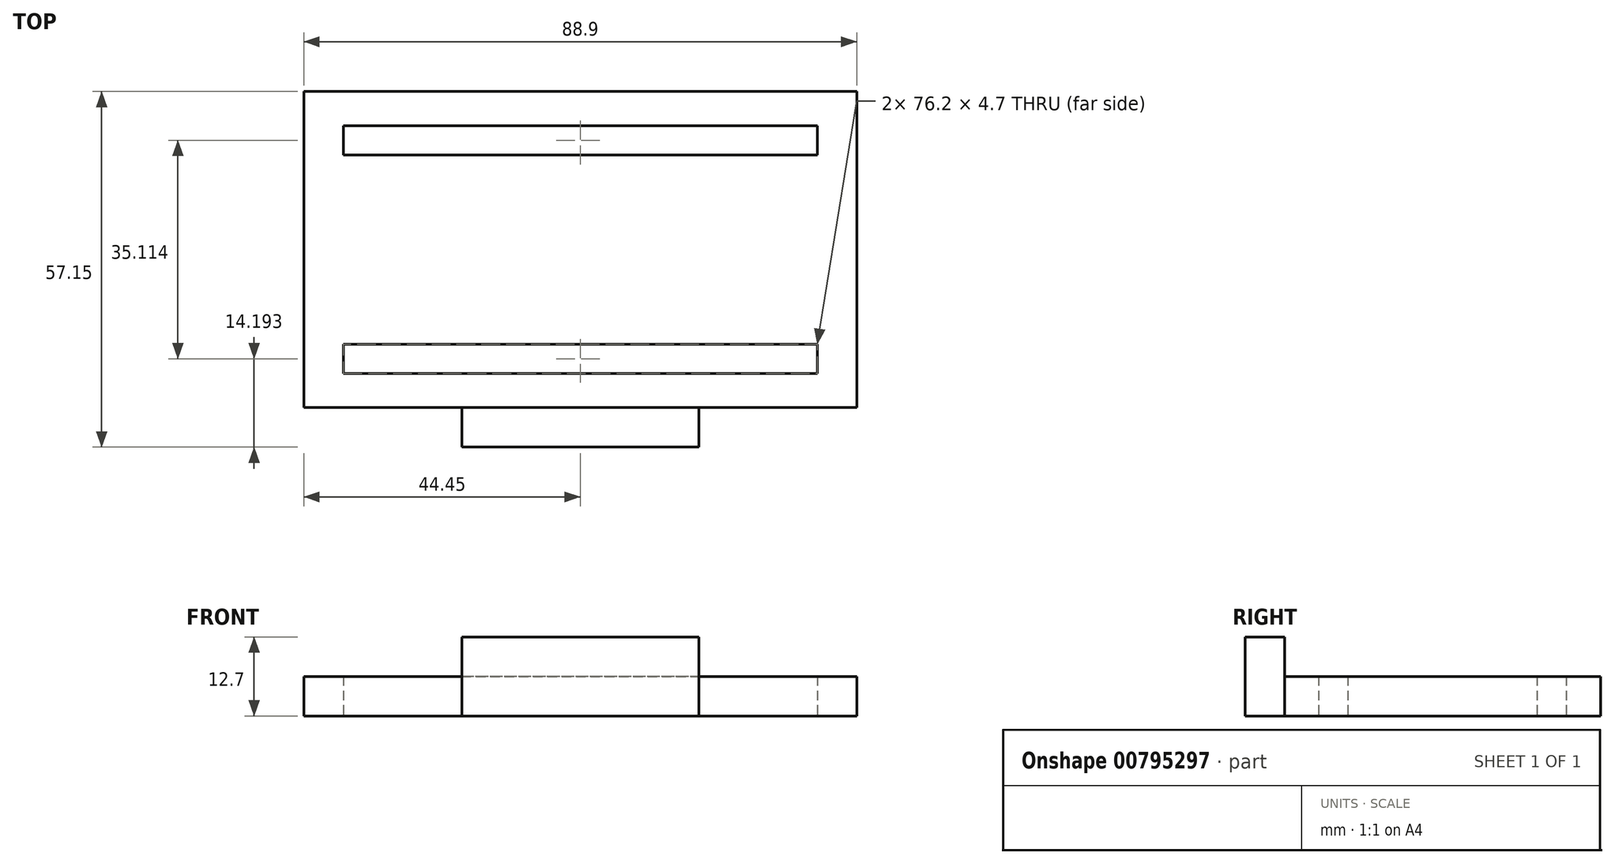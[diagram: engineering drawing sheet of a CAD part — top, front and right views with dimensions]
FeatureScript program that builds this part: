
annotation { "Feature Type Name" : "Feature", "Feature Type Description" : "" }
export const myFeature = defineFeature(function(context is Context, id is Id, definition is map)
    precondition{}
    {
        {
            var Q0;
            Q0=qCreatedBy(makeId("Top.planeOp"),FACE);
            var sketch = newSketch(context, id + "F0", { "sketchPlane" : qUnion([Q0])});
            skLineSegment(sketch, "E0.bottom", {"start": v(44.45, -25.4) * mm, "end": v(-44.45, -25.4) * mm});
            skLineSegment(sketch, "E0.top", {"start": v(44.45, 25.4) * mm, "end": v(-44.45, 25.4) * mm});
            skLineSegment(sketch, "E0.left", {"start": v(44.45, -25.4) * mm, "end": v(44.45, 25.4) * mm});
            skLineSegment(sketch, "E0.right", {"start": v(-44.45, -25.4) * mm, "end": v(-44.45, 25.4) * mm});
            skPoint(sketch, "E0.middle", {"position": v(0, 0) * mm});
            skLineSegment(sketch, "E1.bottom", {"start": v(38.1, 15.2) * mm, "end": v(-38.1, 15.2) * mm});
            skLineSegment(sketch, "E1.top", {"start": v(38.1, 19.9) * mm, "end": v(-38.1, 19.9) * mm});
            skLineSegment(sketch, "E1.left", {"start": v(38.1, 15.2) * mm, "end": v(38.1, 19.9) * mm});
            skLineSegment(sketch, "E1.right", {"start": v(-38.1, 15.2) * mm, "end": v(-38.1, 19.9) * mm});
            skPoint(sketch, "E1.middle", {"position": v(0, 17.56) * mm});
            skLineSegment(sketch, "E2.MirrorCS", {"start": v(-38.1, -15.2) * mm, "end": v(-38.1, -19.9) * mm});
            skLineSegment(sketch, "E3.MirrorCS", {"start": v(38.1, -15.2) * mm, "end": v(38.1, -19.9) * mm});
            skLineSegment(sketch, "E4.MirrorCS", {"start": v(38.1, -19.9) * mm, "end": v(-38.1, -19.9) * mm});
            skPoint(sketch, "E5.MirrorP", {"position": v(0, -17.56) * mm});
            skLineSegment(sketch, "E6.MirrorCS", {"start": v(38.1, -15.2) * mm, "end": v(-38.1, -15.2) * mm});
            skSolve(sketch);
        }
        {
            var Q0;
            Q0=makeQuery(id+"F0.imprint","IMPRINT",FACE,{"disambiguationData":[TD([[makeQuery(id+"F0.imprint","IMPRINT",EDGE,{"derivedFrom":sQuery(id+"F0.wireOp",EDGE,"E0.bottom")}),-1.0]])]});
            extrude(context, id + "F1", {"entities" : qUnion([Q0]), "depth" : 6.35 * mm, "offsetDistance" : 25.4 * mm});
        }
        {
            var Q0;
            Q0=makeQuery(id+"F1.opExtrude","SWEPT_FACE",FACE,{"disambiguationData":[OSD([sQuery(id+"F0.wireOp",EDGE,"E0.bottom")])]});
            var sketch = newSketch(context, id + "F2", { "sketchPlane" : qUnion([Q0])});
            skLineSegment(sketch, "E7.bottom", {"start": v(19.05, 0) * mm, "end": v(-19.05, 0) * mm});
            skLineSegment(sketch, "E7.top", {"start": v(19.05, 6.35) * mm, "end": v(-19.05, 6.35) * mm});
            skLineSegment(sketch, "E7.left", {"start": v(19.05, 0) * mm, "end": v(19.05, 6.35) * mm});
            skLineSegment(sketch, "E7.right", {"start": v(-19.05, 0) * mm, "end": v(-19.05, 6.35) * mm});
            skPoint(sketch, "E7.middle", {"position": v(0, 3.18) * mm});
            skSolve(sketch);
        }
        {
            var Q0;
            Q0=makeQuery(id+"F2.imprint","IMPRINT",FACE,{"disambiguationData":[TD([[makeQuery(id+"F2.imprint","IMPRINT",EDGE,{"derivedFrom":sQuery(id+"F2.wireOp",EDGE,"E7.bottom")}),-1.0]])]});
            extrude(context, id + "F3", {"entities" : qUnion([Q0]), "operationType" : NewBodyOperationType.ADD, "depth" : 6.35 * mm, "offsetDistance" : 25.4 * mm});
        }
        {
            var Q0;
            Q0=makeQuery(id+"F3.boolean.opBoolean","MERGE",FACE,{"derivedFrom":[makeQuery(id+"F1.opExtrude","CAP_FACE",FACE,{"disambiguationData":[OSD([sQuery(id+"F0.wireOp",EDGE,"E0.bottom"),sQuery(id+"F0.wireOp",EDGE,"E0.top"),sQuery(id+"F0.wireOp",EDGE,"E0.left"),sQuery(id+"F0.wireOp",EDGE,"E0.right"),sQuery(id+"F0.wireOp",EDGE,"E1.bottom"),sQuery(id+"F0.wireOp",EDGE,"E1.top"),sQuery(id+"F0.wireOp",EDGE,"E1.left"),sQuery(id+"F0.wireOp",EDGE,"E1.right"),sQuery(id+"F0.wireOp",EDGE,"E2.MirrorCS"),sQuery(id+"F0.wireOp",EDGE,"E3.MirrorCS"),sQuery(id+"F0.wireOp",EDGE,"E4.MirrorCS"),sQuery(id+"F0.wireOp",EDGE,"E6.MirrorCS")])],"isStart":false}),makeQuery(id+"F3.opExtrude","SWEPT_FACE",FACE,{"disambiguationData":[OSD([sQuery(id+"F2.wireOp",EDGE,"E7.top")])]})]});
            var sketch = newSketch(context, id + "F4", { "sketchPlane" : qUnion([Q0])});
            skLineSegment(sketch, "E8.bottom", {"start": v(-19.05, -25.4) * mm, "end": v(19.05, -25.4) * mm});
            skLineSegment(sketch, "E8.top", {"start": v(-19.05, -31.75) * mm, "end": v(19.05, -31.75) * mm});
            skLineSegment(sketch, "E8.left", {"start": v(-19.05, -25.4) * mm, "end": v(-19.05, -31.75) * mm});
            skLineSegment(sketch, "E8.right", {"start": v(19.05, -25.4) * mm, "end": v(19.05, -31.75) * mm});
            skSolve(sketch);
        }
        {
            var Q0;
            Q0 = qSketchRegion(id + "F4", true);
            extrude(context, id + "F5", {"entities" : qUnion([Q0]), "operationType" : NewBodyOperationType.ADD, "depth" : 6.35 * mm, "offsetDistance" : 25.4 * mm});
        }
    });
